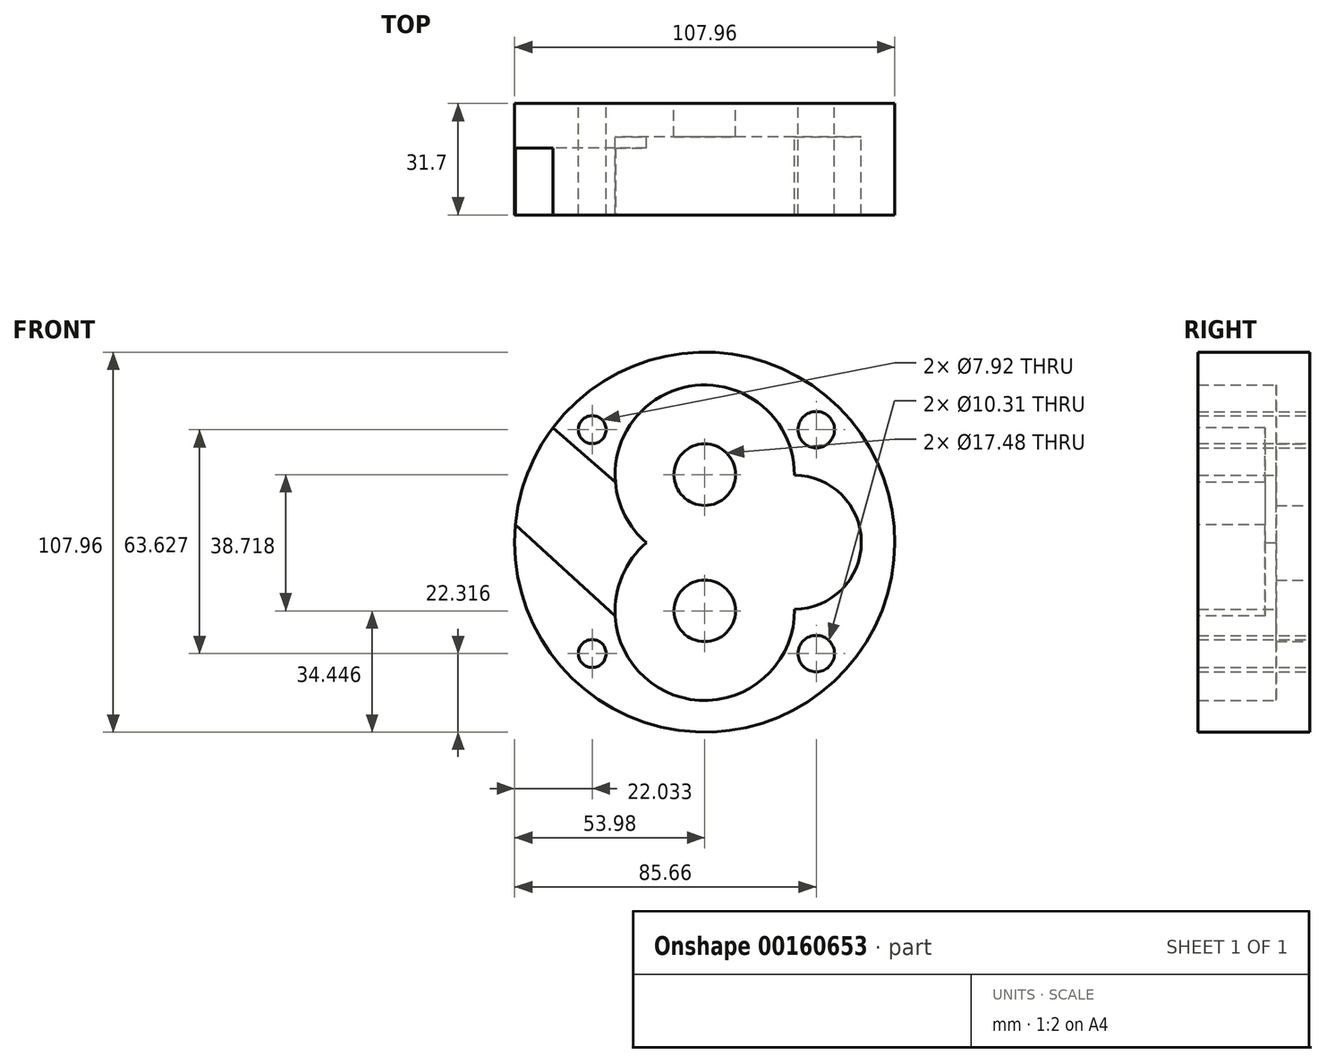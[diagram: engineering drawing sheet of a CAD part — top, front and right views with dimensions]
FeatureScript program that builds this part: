
annotation { "Feature Type Name" : "Feature", "Feature Type Description" : "" }
export const myFeature = defineFeature(function(context is Context, id is Id, definition is map)
    precondition{}
    {
        {
            var Q0;
            Q0=qCreatedBy(makeId("Front.planeOp"),FACE);
            var sketch = newSketch(context, id + "F0", { "sketchPlane" : qUnion([Q0])});
            skCircle(sketch, "E0", {"center": v(0, 0) * mm, "radius": 53.98 * mm});
            skCircle(sketch, "E1", {"center": v(-31.95, 31.96) * mm, "radius": 3.96 * mm});
            skCircle(sketch, "E2", {"center": v(-31.95, -31.66) * mm, "radius": 3.96 * mm});
            skCircle(sketch, "E3", {"center": v(31.68, -31.66) * mm, "radius": 5.16 * mm});
            skCircle(sketch, "E4", {"center": v(31.68, 31.96) * mm, "radius": 5.16 * mm});
            skCircle(sketch, "E5", {"center": v(0, 19.18) * mm, "radius": 8.74 * mm});
            skCircle(sketch, "E6", {"center": v(0, -19.53) * mm, "radius": 8.74 * mm});
            skArc(sketch, "E7", {"start": v(-16.54, -0.17) * mm, "mid": v(0, -45) * mm, "end": v(16.54, -0.17) * mm});
            skArc(sketch, "E8", {"start": v(16.54, -0.17) * mm, "mid": v(0, 44.65) * mm, "end": v(-16.54, -0.17) * mm});
            skLineSegment(sketch, "E9", {"start": v(-24.17, 11.16) * mm, "end": v(-46.56, 27.3) * mm});
            skLineSegment(sketch, "E10", {"start": v(-25.46, -19.56) * mm, "end": v(-53.94, 1.9) * mm});
            skLineSegment(sketch, "E11", {"start": v(0, -19.53) * mm, "end": v(-82.1, -19.56) * mm, "construction": true});
            skArc(sketch, "E12", {"start": v(25.46, -19.05) * mm, "mid": v(44.45, 0) * mm, "end": v(25.46, 19.05) * mm});
            skSolve(sketch);
        }
        {
            var Q0;
            Q0 = qSketchRegion(id + "F0", true);
            extrude(context, id + "F1", {"entities" : qUnion([Q0]), "depth" : 31.7 * mm});
        }
        {
            var Q0;
            Q0=makeQuery(id+"F0.imprint","IMPRINT",FACE,{"disambiguationData":[TD([[makeQuery(id+"F0.imprint","IMPRINT",EDGE,{"derivedFrom":sQuery(id+"F0.wireOp",EDGE,"E5")}),-1.0]])]});
            var Q1;
            {var subQ3=sQuery(id+"F0.wireOp",EDGE,"E12");Q1=makeQuery(id+"F0.imprint","IMPRINT",FACE,{"disambiguationData":[TD([[makeQuery(id+"F0.imprint","IMPRINT",EDGE,{"derivedFrom":subQ3}),1.0]])]});}
            extrude(context, id + "F2", {"entities" : qUnion([Q0, Q1]), "operationType" : NewBodyOperationType.ADD, "depth" : 9.47 * mm});
        }
        {
            var Q0;
            Q0=makeQuery(id+"F1.opExtrude","CAP_FACE",FACE,{"disambiguationData":[OSD([sQuery(id+"F0.wireOp",EDGE,"E0"),sQuery(id+"F0.wireOp",EDGE,"E1"),sQuery(id+"F0.wireOp",EDGE,"E2"),sQuery(id+"F0.wireOp",EDGE,"E3"),sQuery(id+"F0.wireOp",EDGE,"E4"),sQuery(id+"F0.wireOp",EDGE,"E7"),sQuery(id+"F0.wireOp",EDGE,"E8"),sQuery(id+"F0.wireOp",EDGE,"E12")])],"isStart":false});
            var sketch = newSketch(context, id + "F3", { "sketchPlane" : qUnion([Q0])});
            skLineSegment(sketch, "E13", {"start": v(-25.37, 16.95) * mm, "end": v(-43.07, 32.53) * mm});
            skLineSegment(sketch, "E14", {"start": v(-25.42, -21.02) * mm, "end": v(-53.74, 4.99) * mm});
            skSolve(sketch);
        }
        {
            var Q0;
            Q0 = qSketchRegion(id + "F3", true);
            var Q1;
            {var subQ3=sQuery(id+"F3.wireOp",EDGE,"E13");Q1=makeQuery(id+"F3.imprint","IMPRINT",FACE,{"disambiguationData":[TD([[makeQuery(id+"F3.imprint","IMPRINT",EDGE,{"derivedFrom":subQ3}),1.0]])]});}
            extrude(context, id + "F4", {"entities" : qUnion([Q0, Q1]), "operationType" : NewBodyOperationType.REMOVE, "oppositeDirection" : true, "depth" : 19.05 * mm});
        }
    });
